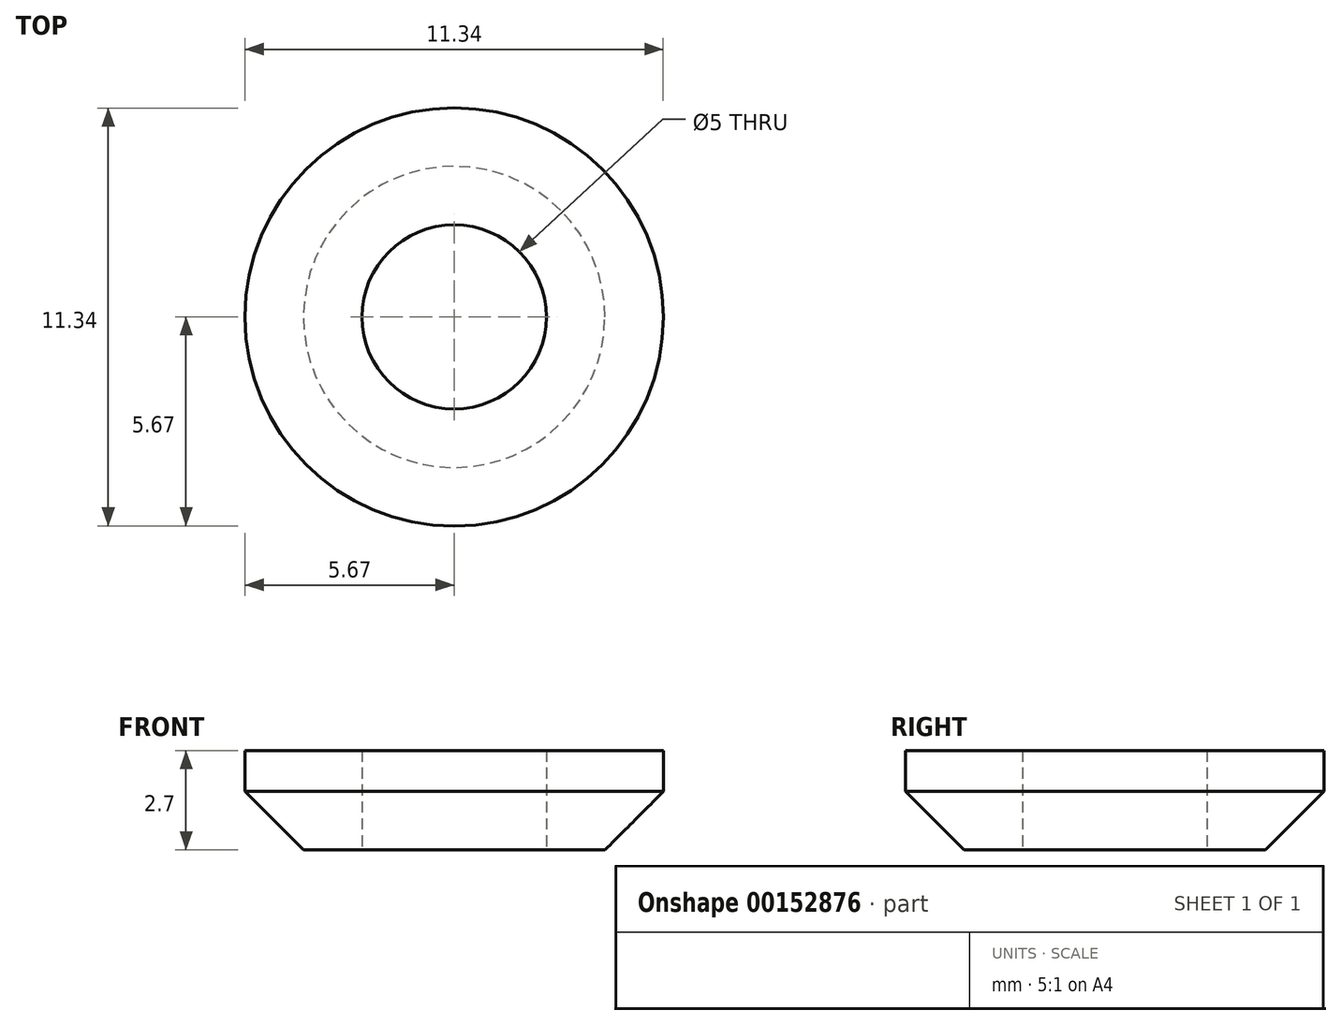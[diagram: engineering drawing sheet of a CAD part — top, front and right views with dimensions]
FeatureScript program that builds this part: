
annotation { "Feature Type Name" : "Feature", "Feature Type Description" : "" }
export const myFeature = defineFeature(function(context is Context, id is Id, definition is map)
    precondition{}
    {
        {
            var Q0;
            Q0=qCreatedBy(makeId("Top.planeOp"),FACE);
            var sketch = newSketch(context, id + "F0", { "sketchPlane" : qUnion([Q0])});
            skCircle(sketch, "E0", {"center": v(0, 0) * mm, "radius": 2.5 * mm});
            skCircle(sketch, "E1", {"center": v(0, 0) * mm, "radius": 5.67 * mm});
            skSolve(sketch);
        }
        {
            var Q0;
            Q0=qSketchRegion(id+"F0",true);
            extrude(context, id + "F1", {"entities" : qUnion([Q0]), "depth" : 2.7 * mm});
        }
        {
            var Q0;
            Q0=makeQuery(id+"F1.opExtrude","CAP_EDGE",EDGE,{"disambiguationData":[OSD([sQuery(id+"F0.wireOp",EDGE,"E1")])],"isStart":true});
            chamfer(context, id + "F2", {"entities" : qUnion([Q0]), "width" : 1.59 * mm, "tangentPropagation" : true});
        }
    });
